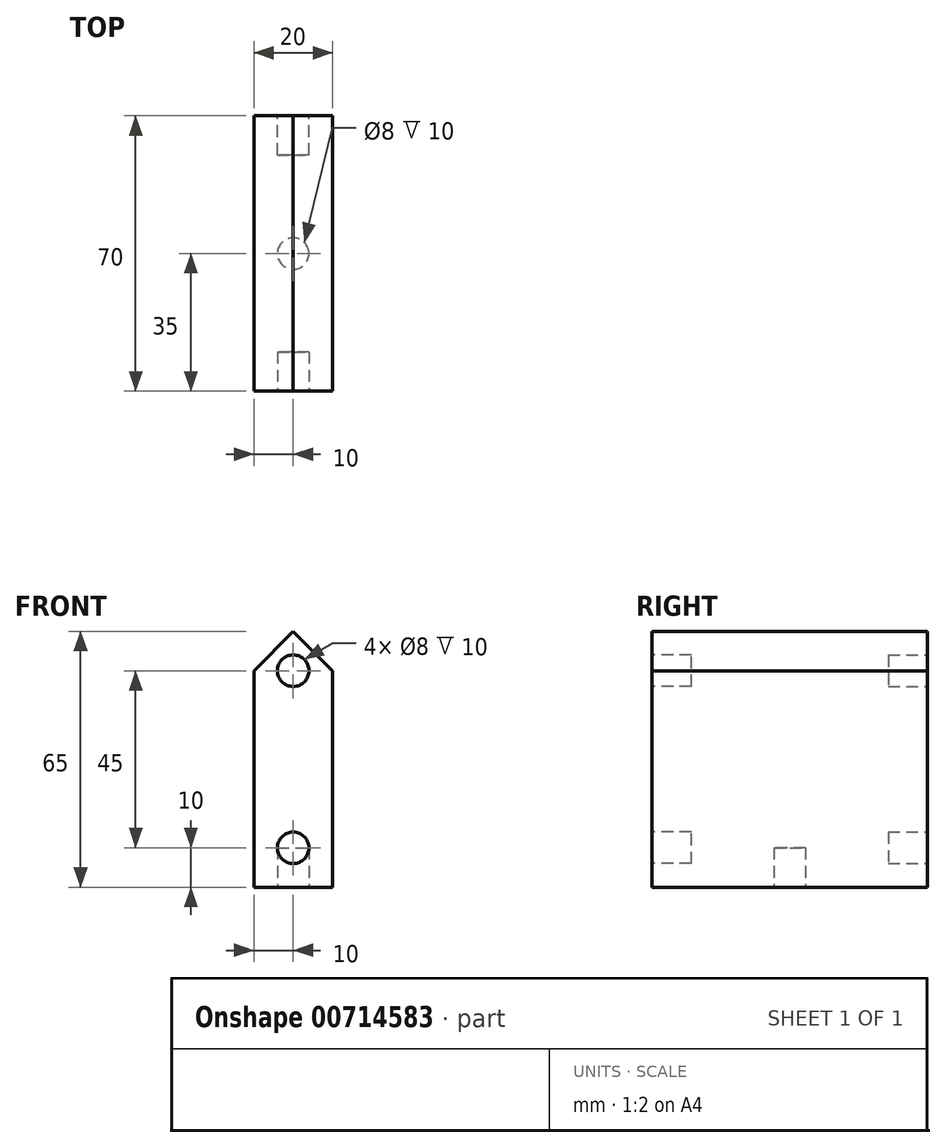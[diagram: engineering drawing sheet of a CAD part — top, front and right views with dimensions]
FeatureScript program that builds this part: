
annotation { "Feature Type Name" : "Feature", "Feature Type Description" : "" }
export const myFeature = defineFeature(function(context is Context, id is Id, definition is map)
    precondition{}
    {
        {
            var Q0;
            Q0=qCreatedBy(makeId("Front.planeOp"),FACE);
            var sketch = newSketch(context, id + "F0", { "sketchPlane" : qUnion([Q0])});
            skLineSegment(sketch, "E0.bottom", {"start": v(-10, 39.5) * mm, "end": v(10, 39.5) * mm});
            skLineSegment(sketch, "E0.top", {"start": v(-10, -39.5) * mm, "end": v(10, -39.5) * mm});
            skLineSegment(sketch, "E0.left", {"start": v(-10, 39.5) * mm, "end": v(-10, -39.5) * mm});
            skLineSegment(sketch, "E0.right", {"start": v(10, 39.5) * mm, "end": v(10, -39.5) * mm});
            skPoint(sketch, "E0.middle", {"position": v(0, 0) * mm});
            skLineSegment(sketch, "E1", {"start": v(0, 39.5) * mm, "end": v(10, 15.5) * mm});
            skLineSegment(sketch, "E2", {"start": v(0, 39.5) * mm, "end": v(-10, 15.5) * mm});
            skLineSegment(sketch, "E3.top", {"start": v(-10, 25.5) * mm, "end": v(10, 25.5) * mm});
            skLineSegment(sketch, "E3.left", {"start": v(-10, 39.5) * mm, "end": v(-10, 25.5) * mm});
            skLineSegment(sketch, "E3.right", {"start": v(10, 39.5) * mm, "end": v(10, 25.5) * mm});
            skLineSegment(sketch, "E4", {"start": v(-10, 15.5) * mm, "end": v(0, 25.5) * mm});
            skLineSegment(sketch, "E5", {"start": v(0, 25.5) * mm, "end": v(10, 15.5) * mm});
            skSolve(sketch);
        }
        {
            var Q0;
            {var subQ1=sQuery(id+"F0.wireOp",EDGE,"E0.top");Q0=makeQuery(id+"F0.imprint","IMPRINT",FACE,{"disambiguationData":[TD([[makeQuery(id+"F0.imprint","IMPRINT",EDGE,{"derivedFrom":subQ1}),1.0]])]});}
            extrude(context, id + "F1", {"entities" : qUnion([Q0]), "depth" : 70 * mm, "offsetDistance" : 25 * mm});
        }
        {
            var Q0;
            Q0=makeQuery(id+"F1.opExtrude","CAP_FACE",FACE,{"disambiguationData":[OSD([sQuery(id+"F0.wireOp",EDGE,"E0.top"),sQuery(id+"F0.wireOp",EDGE,"E0.left"),sQuery(id+"F0.wireOp",EDGE,"E0.right"),sQuery(id+"F0.wireOp",EDGE,"E4"),sQuery(id+"F0.wireOp",EDGE,"E5")])],"isStart":false});
            var sketch = newSketch(context, id + "F2", { "sketchPlane" : qUnion([Q0])});
            skPoint(sketch, "E6", {"position": v(0, -29.5) * mm});
            skCircle(sketch, "E7", {"center": v(0, -29.5) * mm, "radius": 4 * mm});
            skPoint(sketch, "E8", {"position": v(0, 15.5) * mm});
            skCircle(sketch, "E9", {"center": v(0, 15.5) * mm, "radius": 4 * mm});
            skSolve(sketch);
        }
        {
            var Q0;
            Q0=makeQuery(id+"F2.imprint","IMPRINT",FACE,{"disambiguationData":[TD([[makeQuery(id+"F2.imprint","IMPRINT",EDGE,{"derivedFrom":sQuery(id+"F2.wireOp",EDGE,"E7")}),1.0]])]});
            extrude(context, id + "F3", {"entities" : qUnion([Q0]), "operationType" : NewBodyOperationType.REMOVE, "oppositeDirection" : true, "depth" : 10 * mm, "offsetDistance" : 25 * mm});
        }
        {
            var Q0;
            Q0=makeQuery(id+"F1.opExtrude","CAP_FACE",FACE,{"disambiguationData":[OSD([sQuery(id+"F0.wireOp",EDGE,"E0.top"),sQuery(id+"F0.wireOp",EDGE,"E0.left"),sQuery(id+"F0.wireOp",EDGE,"E0.right"),sQuery(id+"F0.wireOp",EDGE,"E4"),sQuery(id+"F0.wireOp",EDGE,"E5")])],"isStart":false});
            var sketch = newSketch(context, id + "F4", { "sketchPlane" : qUnion([Q0])});
            skPoint(sketch, "E10", {"position": v(0, 15.5) * mm});
            skCircle(sketch, "E11", {"center": v(0, 15.5) * mm, "radius": 4 * mm});
            skSolve(sketch);
        }
        {
            var Q0;
            Q0=makeQuery(id+"F4.imprint","IMPRINT",FACE,{"disambiguationData":[TD([[makeQuery(id+"F4.imprint","IMPRINT",EDGE,{"derivedFrom":sQuery(id+"F4.wireOp",EDGE,"E11")}),1.0]])]});
            extrude(context, id + "F5", {"entities" : qUnion([Q0]), "operationType" : NewBodyOperationType.REMOVE, "oppositeDirection" : true, "depth" : 10 * mm, "offsetDistance" : 25 * mm});
        }
        {
            var Q0;
            Q0=makeQuery(id+"F1.opExtrude","CAP_FACE",FACE,{"disambiguationData":[OSD([sQuery(id+"F0.wireOp",EDGE,"E0.top"),sQuery(id+"F0.wireOp",EDGE,"E0.left"),sQuery(id+"F0.wireOp",EDGE,"E0.right"),sQuery(id+"F0.wireOp",EDGE,"E4"),sQuery(id+"F0.wireOp",EDGE,"E5")])],"isStart":true});
            var sketch = newSketch(context, id + "F6", { "sketchPlane" : qUnion([Q0])});
            skPoint(sketch, "E12", {"position": v(0, -29.5) * mm});
            skCircle(sketch, "E13", {"center": v(0, -29.5) * mm, "radius": 4 * mm});
            skSolve(sketch);
        }
        {
            var Q0;
            Q0=makeQuery(id+"F6.imprint","IMPRINT",FACE,{"disambiguationData":[TD([[makeQuery(id+"F6.imprint","IMPRINT",EDGE,{"derivedFrom":sQuery(id+"F6.wireOp",EDGE,"E13")}),1.0]])]});
            extrude(context, id + "F7", {"entities" : qUnion([Q0]), "operationType" : NewBodyOperationType.REMOVE, "oppositeDirection" : true, "depth" : 10 * mm, "offsetDistance" : 25 * mm});
        }
        {
            var Q0;
            Q0=makeQuery(id+"F1.opExtrude","CAP_FACE",FACE,{"disambiguationData":[OSD([sQuery(id+"F0.wireOp",EDGE,"E0.top"),sQuery(id+"F0.wireOp",EDGE,"E0.left"),sQuery(id+"F0.wireOp",EDGE,"E0.right"),sQuery(id+"F0.wireOp",EDGE,"E4"),sQuery(id+"F0.wireOp",EDGE,"E5")])],"isStart":true});
            var sketch = newSketch(context, id + "F8", { "sketchPlane" : qUnion([Q0])});
            skPoint(sketch, "E14", {"position": v(0, 15.5) * mm});
            skCircle(sketch, "E15", {"center": v(0, 15.5) * mm, "radius": 4 * mm});
            skSolve(sketch);
        }
        {
            var Q0;
            Q0=makeQuery(id+"F8.imprint","IMPRINT",FACE,{"disambiguationData":[TD([[makeQuery(id+"F8.imprint","IMPRINT",EDGE,{"derivedFrom":sQuery(id+"F8.wireOp",EDGE,"E15")}),1.0]])]});
            extrude(context, id + "F9", {"entities" : qUnion([Q0]), "operationType" : NewBodyOperationType.REMOVE, "oppositeDirection" : true, "depth" : 10 * mm, "offsetDistance" : 25 * mm});
        }
        {
            var Q0;
            Q0=makeQuery(id+"F1.opExtrude","SWEPT_FACE",FACE,{"disambiguationData":[OSD([sQuery(id+"F0.wireOp",EDGE,"E0.top")])]});
            var sketch = newSketch(context, id + "F10", { "sketchPlane" : qUnion([Q0])});
            skPoint(sketch, "E16", {"position": v(0, 35) * mm});
            skCircle(sketch, "E17", {"center": v(0, 35) * mm, "radius": 4 * mm});
            skSolve(sketch);
        }
        {
            var Q0;
            Q0=makeQuery(id+"F10.imprint","IMPRINT",FACE,{"disambiguationData":[TD([[makeQuery(id+"F10.imprint","IMPRINT",EDGE,{"derivedFrom":sQuery(id+"F10.wireOp",EDGE,"E17")}),1.0]])]});
            extrude(context, id + "F11", {"entities" : qUnion([Q0]), "operationType" : NewBodyOperationType.REMOVE, "oppositeDirection" : true, "depth" : 10 * mm, "offsetDistance" : 25 * mm});
        }
    });
